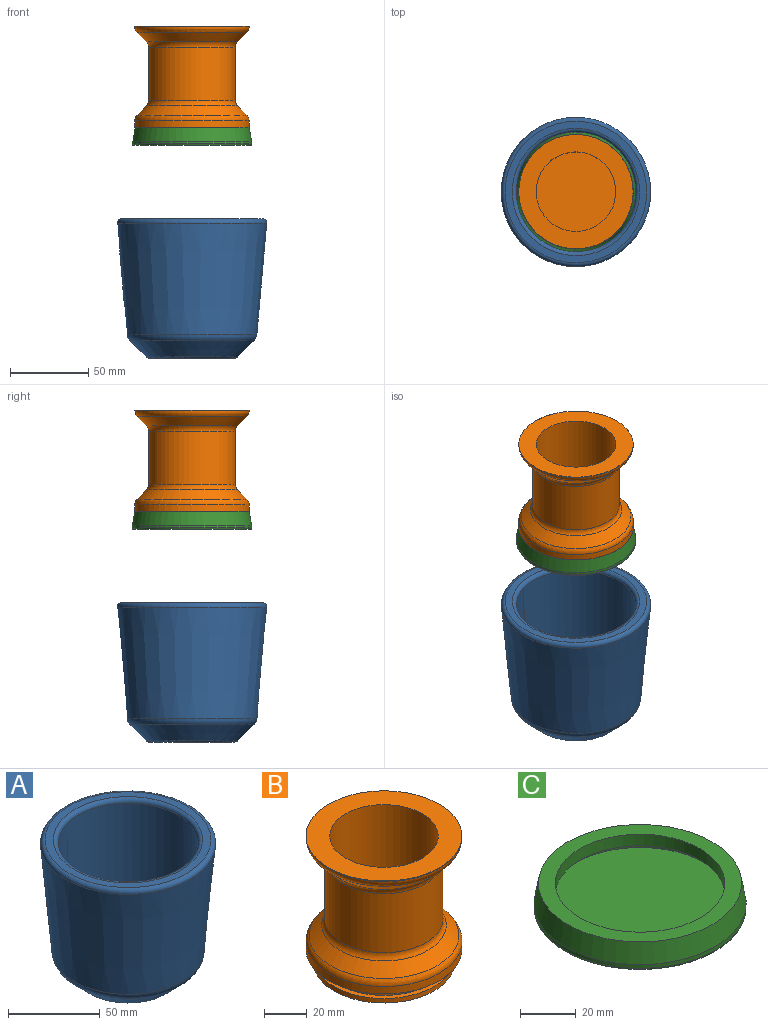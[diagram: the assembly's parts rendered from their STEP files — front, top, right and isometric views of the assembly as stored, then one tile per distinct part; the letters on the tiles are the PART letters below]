
ASSEMBLY  parts=3 mates=4
PART A: 69 faces, bbox 103.3x103.3x88.9 mm
  f0: cylinder r=38.1mm len=76.2mm, axis (0,0,1), area 17633.4mm2, adj f1,f3,f5,f7,f9,f16,f18,f35
  f1: cone r=38.1mm half-angle=45deg, axis (0,0,1), area 976mm2, adj f0,f4,f26,f27,f47,f58,f63,f68
  f2: cone r=38.1mm half-angle=45deg, axis (0,0,1), area 0mm2, adj f4,f53,f54
  f3: cone r=38.1mm half-angle=45deg, axis (0,0,1), area 976mm2, adj f0,f4,f30,f31,f38,f57,f65,f67
  f4: cone r=27.94mm half-angle=60deg, axis (0,0,-1), area 2384.1mm2, adj f1,f2,f3,f5,f6,f8,f20,f21
  f5: cone r=38.1mm half-angle=45deg, axis (0,0,1), area 976mm2, adj f0,f4,f23,f24,f37,f48,f64,f66
  f6: cone r=38.1mm half-angle=45deg, axis (0,0,1), area 0mm2, adj f4,f43,f44
  f7: cone r=38.1mm half-angle=45deg, axis (0,0,1), area 0mm2, adj f0,f55,f60
  f8: cone r=38.1mm half-angle=45deg, axis (0,0,1), area 0mm2, adj f4,f33,f34
  f9: cone r=38.1mm half-angle=45deg, axis (0,0,1), area 0mm2, adj f0,f45,f50
  f10: plane 55.05x54.61mm, normal (0,0,-1), area 2354.7mm2, adj f11,f21,f22,f24,f25,f27,f28,f29
  f11: torus R=27.52mm, axis (0,0,1), area 345.6mm2, adj f10,f14,f22,f23,f24,f25,f26,f27
  f12: cone r=41.27mm half-angle=5deg, axis (0,0,1), area 20005.4mm2, adj f15,f17
  f13: plane 90.34x90.34mm, normal (0,0,1), area 1221.1mm2, adj f16,f17
  f14: cone r=41.27mm half-angle=45deg, axis (0,0,1), area 3162.4mm2, adj f11,f15
  f15: torus R=35.15mm, axis (0,0,-1), area 1136.2mm2, adj f12,f14
  f16: torus R=40.64mm, axis (0,0,1), area 978.3mm2, adj f0,f13
  f17: torus R=45.17mm, axis (0,0,1), area 1239.3mm2, adj f12,f13
  f18: cone r=38.1mm half-angle=45deg, axis (0,0,1), area 0mm2, adj f0,f35,f40
  f19: plane 1.68x1.68mm, normal (0,0,1), area 2.2mm2, adj f20
  f20: torus R=0.84mm, axis (0,0,1), area 343mm2, adj f4,f19,f35,f37,f38,f40,f41,f42
  f21: cylinder r=28.57mm len=8.39mm, axis (0,0,1), area 27.6mm2, adj f4,f10,f22,f24
  f22: cylinder r=0.64mm len=3.28mm, axis (0,0,1), area 5.8mm2, adj f4,f10,f11,f21,f23
  f23: cylinder r=29.84mm len=8.76mm, axis (0,0,1), area 22.1mm2, adj f4,f5,f11,f22,f24
  f24: cylinder r=0.64mm len=3.27mm, axis (0,0,1), area 5.8mm2, adj f4,f5,f10,f11,f21,f23
  f25: cylinder r=0.64mm len=3.28mm, axis (0,0,1), area 5.8mm2, adj f4,f10,f11,f26,f28
  f26: cylinder r=29.84mm len=7.6mm, axis (0,0,1), area 22.1mm2, adj f1,f4,f11,f25,f27
  f27: cylinder r=0.64mm len=3.27mm, axis (0,0,1), area 5.8mm2, adj f1,f4,f10,f11,f26,f28
  f28: cylinder r=28.57mm len=7.27mm, axis (0,0,1), area 27.6mm2, adj f4,f10,f25,f27
  f29: cylinder r=0.64mm len=3.28mm, axis (0,0,1), area 5.8mm2, adj f4,f10,f11,f30,f32
  f30: cylinder r=29.84mm len=7.58mm, axis (0,0,1), area 22.1mm2, adj f3,f4,f11,f29,f31
  f31: cylinder r=0.64mm len=3.27mm, axis (0,0,1), area 5.8mm2, adj f3,f4,f10,f11,f30,f32
  f32: cylinder r=28.57mm len=7.26mm, axis (0,0,1), area 27.6mm2, adj f4,f10,f29,f31
  f33: plane 0.5x0.35mm, normal (-0.54,-0.46,-0.71), area 0mm2, adj f8,f34,f36
  f34: plane 0.5x0.35mm, normal (-0.46,-0.54,-0.71), area 0mm2, adj f8,f33,f39
  f35: bspline ~26.21x26.2mm, area 4.7mm2, adj f0,f18,f20,f40,f66
  f36: bspline ~14.74x14.72mm, area 10.3mm2, adj f4,f33,f37,f39
  f37: plane 20.09x20.09mm, normal (0.71,-0.71,0), area 82.2mm2, adj f4,f5,f20,f36,f66
  f38: plane 20.09x20.09mm, normal (-0.71,0.71,0), area 82.2mm2, adj f3,f4,f20,f39,f65
  f39: bspline ~14.74x14.72mm, area 10.3mm2, adj f4,f34,f36,f38
  f40: bspline ~26.21x26.2mm, area 4.7mm2, adj f0,f18,f20,f35,f65
  f41: bspline ~1.65x1.63mm, area 0.6mm2, adj f20,f42,f66
  f42: bspline ~1.65x1.63mm, area 0.6mm2, adj f20,f41,f65
  f43: plane 0.5x0.48mm, normal (0.67,-0.23,-0.71), area 0mm2, adj f6,f44,f46
  f44: plane 0.5x0.48mm, normal (0.7,-0.13,-0.71), area 0mm2, adj f6,f43,f49
  f45: bspline ~52.35x46mm, area 4.7mm2, adj f0,f9,f20,f50,f63
  f46: bspline ~36.38x26.71mm, area 10.3mm2, adj f4,f43,f47,f49
  f47: plane 27.44x11.09mm, normal (0.26,0.97,0), area 82.1mm2, adj f1,f4,f20,f46,f63
  f48: plane 27.44x11.09mm, normal (-0.26,-0.97,0), area 82.1mm2, adj f4,f5,f20,f49,f64
  f49: bspline ~35.96x28.26mm, area 10.3mm2, adj f4,f44,f46,f48
  f50: bspline ~52.07x47.05mm, area 4.7mm2, adj f0,f9,f20,f45,f64
  f51: bspline ~32.42x12.21mm, area 0.6mm2, adj f20,f52,f63
  f52: bspline ~32.08x13.49mm, area 0.6mm2, adj f20,f51,f64
  f53: plane 0.5x0.48mm, normal (-0.13,0.7,-0.71), area 0mm2, adj f2,f54,f56
  f54: plane 0.5x0.48mm, normal (-0.23,0.67,-0.71), area 0mm2, adj f2,f53,f59
  f55: bspline ~52.07x47.05mm, area 4.7mm2, adj f0,f7,f20,f60,f67
  f56: bspline ~35.96x28.26mm, area 10.3mm2, adj f4,f53,f57,f59
  f57: plane 27.44x11.09mm, normal (-0.97,-0.26,0), area 82.1mm2, adj f3,f4,f20,f56,f67
  f58: plane 27.44x11.09mm, normal (0.97,0.26,0), area 82.1mm2, adj f1,f4,f20,f59,f68
  f59: bspline ~36.38x26.71mm, area 10.3mm2, adj f4,f54,f56,f58
  f60: bspline ~52.35x46mm, area 4.7mm2, adj f0,f7,f20,f55,f68
  f61: bspline ~32.08x13.49mm, area 0.6mm2, adj f20,f62,f67
  f62: bspline ~32.42x12.21mm, area 0.6mm2, adj f20,f61,f68
  f63: bspline ~36.97x10.3mm, area 22.5mm2, adj f1,f20,f45,f47,f51
  f64: bspline ~36.84x10.36mm, area 22.5mm2, adj f5,f20,f48,f50,f52
  f65: bspline ~28.67x28.51mm, area 22.5mm2, adj f3,f20,f38,f40,f42
  f66: bspline ~28.67x28.51mm, area 22.5mm2, adj f5,f20,f35,f37,f41
  f67: bspline ~36.84x10.36mm, area 22.5mm2, adj f3,f20,f55,f57,f61
  f68: bspline ~36.97x10.3mm, area 22.5mm2, adj f1,f20,f58,f60,f62
PART B: 17 faces, bbox 79x79x72.4 mm
  f0: cylinder r=33.02mm len=66.04mm, axis (0,0,-1), area 527mm2, adj f1,f2
  f1: plane 66.04x66.04mm, normal (0,0,1), area 506.7mm2, adj f0,f3
  f2: plane 66.04x66.04mm, normal (0,0,-1), area 3425.3mm2, adj f0
  f3: cylinder r=30.48mm len=60.96mm, axis (0,0,-1), area 972.9mm2, adj f1,f5
  f4: cylinder r=36.51mm len=73.03mm, axis (0,0,-1), area 974mm2, adj f5,f14
  f5: plane 73.03x73.03mm, normal (0,0,-1), area 1269.6mm2, adj f3,f4
  f6: cone r=36.51mm half-angle=45deg, axis (0,0,-1), area 1685.2mm2, adj f13,f14
  f7: cylinder r=27.62mm len=55.25mm, axis (0,0,-1), area 5882.1mm2, adj f12,f13
  f8: cone r=27.62mm half-angle=45deg, axis (0,0,1), area 1685.2mm2, adj f11,f12
  f9: cylinder r=36.51mm len=73.03mm, axis (0,0,-1), area 100mm2, adj f10,f11
  f10: plane 73.03x73.03mm, normal (0,0,1), area 2161.4mm2, adj f9,f15
  f11: torus R=31.43mm, axis (0,0,-1), area 902.6mm2, adj f8,f9
  f12: torus R=32.7mm, axis (0,0,1), area 705.2mm2, adj f7,f8
  f13: torus R=32.7mm, axis (0,0,1), area 705.2mm2, adj f6,f7
  f14: torus R=31.43mm, axis (0,0,-1), area 902.6mm2, adj f4,f6
  f15: cylinder r=25.4mm len=50.8mm, axis (0,0,1), area 8107.3mm2, adj f10,f16
  f16: plane 50.8x50.8mm, normal (0,0,1), area 2026.8mm2, adj f15
PART C: 9 faces, bbox 82.5x82.5x11.4 mm
  f0: cylinder r=38.1mm len=76.2mm, axis (0,0,-1), area 395.2mm2, adj f2,f8
  f1: plane 74.42x74.42mm, normal (0,0,-1), area 4350mm2, adj f8
  f2: cone r=38.1mm half-angle=10deg, axis (0,0,-1), area 2116.5mm2, adj f0,f3
  f3: plane 73.07x73.07mm, normal (0,0,1), area 1274.2mm2, adj f2,f4
  f4: cylinder r=30.48mm len=60.96mm, axis (0,0,1), area 972.9mm2, adj f3,f5
  f5: plane 66.04x66.04mm, normal (0,0,-1), area 506.7mm2, adj f4,f6
  f6: cylinder r=33.02mm len=66.04mm, axis (0,0,-1), area 527mm2, adj f5,f7
  f7: plane 66.04x66.04mm, normal (0,0,1), area 3425.3mm2, adj f6
  f8: torus R=37.21mm, axis (0,0,1), area 331.5mm2, adj f0,f1
PLACE A t=(-88.09,-30.81,-30.35)mm
PLACE B t=(-88.09,-30.81,-8.87)mm
PLACE C t=(-88.09,-30.81,-8.87)mm
MATE slider A.f0 <-> C.f0  axis (0,0,1) through (-88.09,-30.81,6.48)mm
MATE planar B.f0 <-> C.f6  axis (0,0,-1) through (-88.09,-30.81,96.54)mm
MATE cylindrical B.f0 <-> C.f6  axis (0,0,-1) through (-88.09,-30.81,97.81)mm
MATE cylindrical B.f0 <-> C.f6  axis (0,0,-1) through (-88.09,-30.81,96.54)mm
